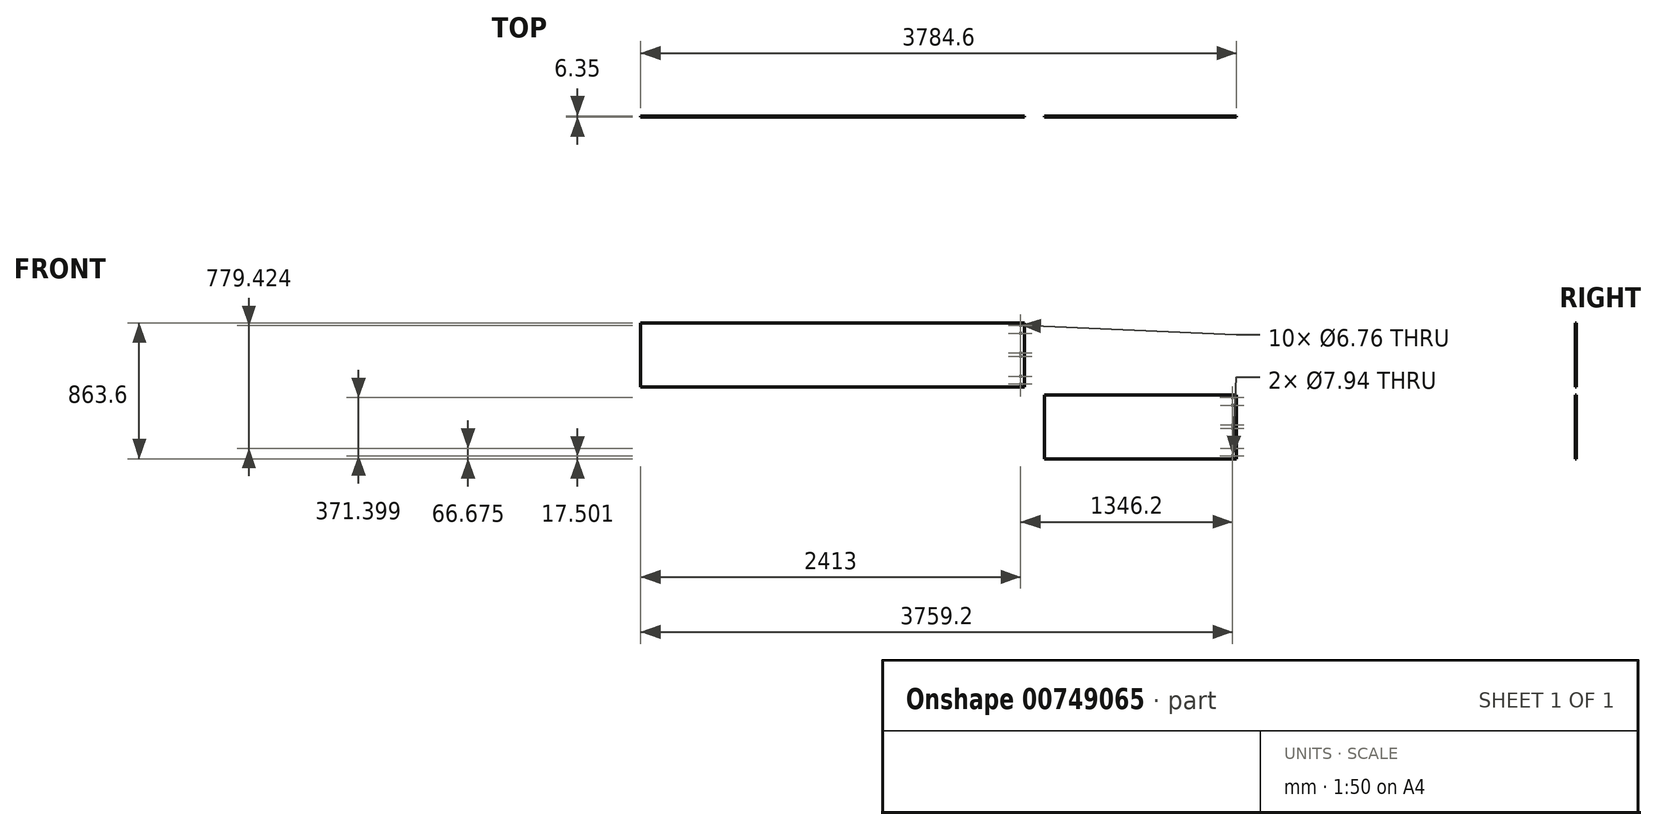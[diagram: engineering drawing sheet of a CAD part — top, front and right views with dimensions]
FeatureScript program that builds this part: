
annotation { "Feature Type Name" : "Feature", "Feature Type Description" : "" }
export const myFeature = defineFeature(function(context is Context, id is Id, definition is map)
    precondition{}
    {
        {
            var Q0;
            Q0=qCreatedBy(makeId("Front.planeOp"),FACE);
            var sketch = newSketch(context, id + "F0", { "sketchPlane" : qUnion([Q0])});
            skLineSegment(sketch, "E0.bottom", {"start": v(0, 0) * mm, "end": v(-2438.4, 0) * mm});
            skLineSegment(sketch, "E0.top", {"start": v(0, 406.4) * mm, "end": v(-2438.4, 406.4) * mm});
            skLineSegment(sketch, "E0.left", {"start": v(0, 0) * mm, "end": v(0, 406.4) * mm});
            skLineSegment(sketch, "E0.right", {"start": v(-2438.4, 0) * mm, "end": v(-2438.4, 406.4) * mm});
            skLineSegment(sketch, "E1", {"start": v(0, 203.2) * mm, "end": v(-2438.4, 203.2) * mm, "construction": true});
            skPoint(sketch, "E2", {"position": v(-25.4, 339.73) * mm});
            skPoint(sketch, "E3", {"position": v(-25.4, 388.9) * mm});
            skPoint(sketch, "E4.MirrorP", {"position": v(-25.4, -388.9) * mm});
            skPoint(sketch, "E5.MirrorP", {"position": v(-25.4, -339.72) * mm});
            skPoint(sketch, "E6.MirrorP", {"position": v(-25.4, 66.67) * mm});
            skPoint(sketch, "E7.MirrorP", {"position": v(-25.4, 17.5) * mm});
            skLineSegment(sketch, "E8", {"start": v(0, 192.2) * mm, "end": v(-2438.4, 192.2) * mm, "construction": true});
            skPoint(sketch, "E9", {"position": v(-25.4, 192.2) * mm});
            skPoint(sketch, "E10.MirrorP", {"position": v(-25.4, 214.2) * mm});
            skLineSegment(sketch, "E11", {"start": v(0, 317.5) * mm, "end": v(-510.55, 317.5) * mm, "construction": true});
            skLineSegment(sketch, "E12", {"start": v(0, 355.6) * mm, "end": v(-513.55, 355.6) * mm, "construction": true});
            skLineSegment(sketch, "E13.MirrorCS", {"start": v(0, 88.9) * mm, "end": v(-510.55, 88.9) * mm, "construction": true});
            skLineSegment(sketch, "E14.MirrorCS", {"start": v(0, 50.8) * mm, "end": v(-513.55, 50.8) * mm, "construction": true});
            skSolve(sketch);
        }
        {
            var Q0;
            Q0 = qSketchRegion(id + "F0", true);
            extrude(context, id + "F1", {"entities" : qUnion([Q0]), "depth" : 6.35 * mm, "offsetDistance" : 25.4 * mm});
        }
        {
            var Q0;
            Q0=qCreatedBy(makeId("Front.planeOp"),FACE);
            var sketch = newSketch(context, id + "F2", { "sketchPlane" : qUnion([Q0])});
            skLineSegment(sketch, "E15.bottom", {"start": v(127, -50.8) * mm, "end": v(1346.2, -50.8) * mm});
            skLineSegment(sketch, "E15.top", {"start": v(127, -457.2) * mm, "end": v(1346.2, -457.2) * mm});
            skLineSegment(sketch, "E15.left", {"start": v(127, -50.8) * mm, "end": v(127, -457.2) * mm});
            skLineSegment(sketch, "E15.right", {"start": v(1346.2, -50.8) * mm, "end": v(1346.2, -457.2) * mm});
            skLineSegment(sketch, "E16", {"start": v(127, -254) * mm, "end": v(1346.2, -254) * mm, "construction": true});
            skPoint(sketch, "E17", {"position": v(1320.8, -68.3) * mm});
            skPoint(sketch, "E18.MirrorP", {"position": v(1320.8, -439.7) * mm});
            skPoint(sketch, "E19", {"position": v(1320.8, -117.47) * mm});
            skPoint(sketch, "E20.MirrorP", {"position": v(1320.8, -390.52) * mm});
            skLineSegment(sketch, "E21", {"start": v(1346.2, -265) * mm, "end": v(616.8, -265) * mm, "construction": true});
            skPoint(sketch, "E22", {"position": v(1320.8, -265) * mm});
            skPoint(sketch, "E23.MirrorP", {"position": v(1320.8, -243) * mm});
            skSolve(sketch);
        }
        {
            var Q0;
            Q0 = qSketchRegion(id + "F2", true);
            extrude(context, id + "F3", {"entities" : qUnion([Q0]), "depth" : 6.35 * mm, "offsetDistance" : 25.4 * mm});
        }
        {
            var Q0;
            Q0=sQuery(id+"F2.wireOp",VERTEX,"E17");
            var Q1;
            Q1=sQuery(id+"F2.wireOp",VERTEX,"E18.MirrorP");
            var Q2;
            Q2=makeQuery(id+"F3.opExtrude","SWEPT_BODY",BODY,{"disambiguationData":[OSD([sQuery(id+"F2.wireOp",EDGE,"E15.bottom"),sQuery(id+"F2.wireOp",EDGE,"E15.top"),sQuery(id+"F2.wireOp",EDGE,"E15.left"),sQuery(id+"F2.wireOp",EDGE,"E15.right")])]});
            hole(context, id + "F4", {"style" : HoleStyle.SIMPLE, "endStyle" : HoleEndStyle.BLIND, "oppositeDirection" : true, "standardTappedOrClearance" : lookupTablePath({ "standard" : "ANSI", "engagement" : "75%", "pitch" : "16 tpi", "size" : "3/8", "type" : "Tapped" }), "standardBlindInLast" : lookupTablePath({ "standard" : "ANSI", "engagement" : "75%", "pitch" : "16 tpi", "size" : "3/8", "type" : "Tapped" }), "holeDiameter" : 7.94 * mm, "majorDiameter" : 9.52 * mm, "showTappedDepth" : true, "holeDepth" : 20.62 * mm, "isTappedThrough" : true, "tappedDepth" : 15.86 * mm, "tapClearance" : 3, "locations" : qUnion([Q0, Q1]), "scope" : qUnion([Q2])});
        }
        {
            var Q0;
            Q0=sQuery(id+"F2.wireOp",VERTEX,"E17");
            var Q1;
            Q1=sQuery(id+"F2.wireOp",VERTEX,"E19");
            var Q2;
            Q2=sQuery(id+"F2.wireOp",VERTEX,"E20.MirrorP");
            var Q3;
            Q3=sQuery(id+"F2.wireOp",VERTEX,"E18.MirrorP");
            var Q4;
            Q4=makeQuery(id+"F3.opExtrude","SWEPT_BODY",BODY,{"disambiguationData":[OSD([sQuery(id+"F2.wireOp",EDGE,"E15.bottom"),sQuery(id+"F2.wireOp",EDGE,"E15.top"),sQuery(id+"F2.wireOp",EDGE,"E15.left"),sQuery(id+"F2.wireOp",EDGE,"E15.right")])]});
            hole(context, id + "F5", {"style" : HoleStyle.SIMPLE, "endStyle" : HoleEndStyle.BLIND, "oppositeDirection" : true, "standardTappedOrClearance" : lookupTablePath({ "standard" : "ANSI", "fit" : "Normal (ASME)", "size" : "1/4", "type" : "Clearance" }), "standardBlindInLast" : lookupTablePath({ "fit" : "Free", "standard" : "ANSI", "size" : "1/4", "type" : "Clearance" }), "holeDiameter" : 6.76 * mm, "majorDiameter" : 6.35 * mm, "holeDepth" : 19.67 * mm, "isTappedThrough" : true, "tappedDepth" : 15.86 * mm, "tapClearance" : 3, "locations" : qUnion([Q0, Q1, Q2, Q3]), "scope" : qUnion([Q4])});
        }
        {
            var Q0;
            Q0=sQuery(id+"F0.wireOp",VERTEX,"E3");
            var Q1;
            Q1=sQuery(id+"F0.wireOp",VERTEX,"E2");
            var Q2;
            Q2=sQuery(id+"F0.wireOp",VERTEX,"E6.MirrorP");
            var Q3;
            Q3=sQuery(id+"F0.wireOp",VERTEX,"E7.MirrorP");
            var Q4;
            Q4=makeQuery(id+"F1.opExtrude","SWEPT_BODY",BODY,{"disambiguationData":[OSD([sQuery(id+"F0.wireOp",EDGE,"E0.bottom"),sQuery(id+"F0.wireOp",EDGE,"E0.top"),sQuery(id+"F0.wireOp",EDGE,"E0.left"),sQuery(id+"F0.wireOp",EDGE,"E0.right")])]});
            hole(context, id + "F6", {"style" : HoleStyle.SIMPLE, "endStyle" : HoleEndStyle.BLIND, "oppositeDirection" : true, "standardTappedOrClearance" : lookupTablePath({ "standard" : "ANSI", "fit" : "Normal (ASME)", "size" : "1/4", "type" : "Clearance" }), "standardBlindInLast" : lookupTablePath({ "fit" : "Free", "standard" : "ANSI", "size" : "1/4", "type" : "Clearance" }), "holeDiameter" : 6.76 * mm, "majorDiameter" : 6.35 * mm, "holeDepth" : 19.68 * mm, "isTappedThrough" : true, "tappedDepth" : 15.88 * mm, "tapClearance" : 3, "locations" : qUnion([Q0, Q1, Q2, Q3]), "scope" : qUnion([Q4])});
        }
        {
            var Q0;
            Q0=sQuery(id+"F0.wireOp",VERTEX,"E10.MirrorP");
            var Q1;
            Q1=sQuery(id+"F0.wireOp",VERTEX,"E9");
            var Q2;
            Q2=makeQuery(id+"F1.opExtrude","SWEPT_BODY",BODY,{"disambiguationData":[OSD([sQuery(id+"F0.wireOp",EDGE,"E0.bottom"),sQuery(id+"F0.wireOp",EDGE,"E0.top"),sQuery(id+"F0.wireOp",EDGE,"E0.left"),sQuery(id+"F0.wireOp",EDGE,"E0.right")])]});
            hole(context, id + "F7", {"style" : HoleStyle.SIMPLE, "endStyle" : HoleEndStyle.BLIND, "oppositeDirection" : true, "standardTappedOrClearance" : lookupTablePath({ "standard" : "ANSI", "fit" : "Normal (ASME)", "size" : "1/4", "type" : "Clearance" }), "standardBlindInLast" : lookupTablePath({ "fit" : "Free", "standard" : "ANSI", "size" : "1/4", "type" : "Clearance" }), "holeDiameter" : 6.76 * mm, "majorDiameter" : 6.35 * mm, "holeDepth" : 19.68 * mm, "isTappedThrough" : true, "tappedDepth" : 15.88 * mm, "tapClearance" : 3, "locations" : qUnion([Q0, Q1]), "scope" : qUnion([Q2])});
        }
        {
            var Q0;
            Q0=sQuery(id+"F2.wireOp",VERTEX,"E23.MirrorP");
            var Q1;
            Q1=sQuery(id+"F2.wireOp",VERTEX,"E22");
            var Q2;
            Q2=makeQuery(id+"F3.opExtrude","SWEPT_BODY",BODY,{"disambiguationData":[OSD([sQuery(id+"F2.wireOp",EDGE,"E15.bottom"),sQuery(id+"F2.wireOp",EDGE,"E15.top"),sQuery(id+"F2.wireOp",EDGE,"E15.left"),sQuery(id+"F2.wireOp",EDGE,"E15.right")])]});
            hole(context, id + "F8", {"style" : HoleStyle.SIMPLE, "endStyle" : HoleEndStyle.BLIND, "oppositeDirection" : true, "standardTappedOrClearance" : lookupTablePath({ "standard" : "ANSI", "fit" : "Normal (ASME)", "size" : "1/4", "type" : "Clearance" }), "standardBlindInLast" : lookupTablePath({ "fit" : "Free", "standard" : "ANSI", "size" : "1/4", "type" : "Clearance" }), "holeDiameter" : 6.76 * mm, "majorDiameter" : 6.35 * mm, "holeDepth" : 19.68 * mm, "isTappedThrough" : true, "tappedDepth" : 15.88 * mm, "tapClearance" : 3, "locations" : qUnion([Q0, Q1]), "scope" : qUnion([Q2])});
        }
    });
